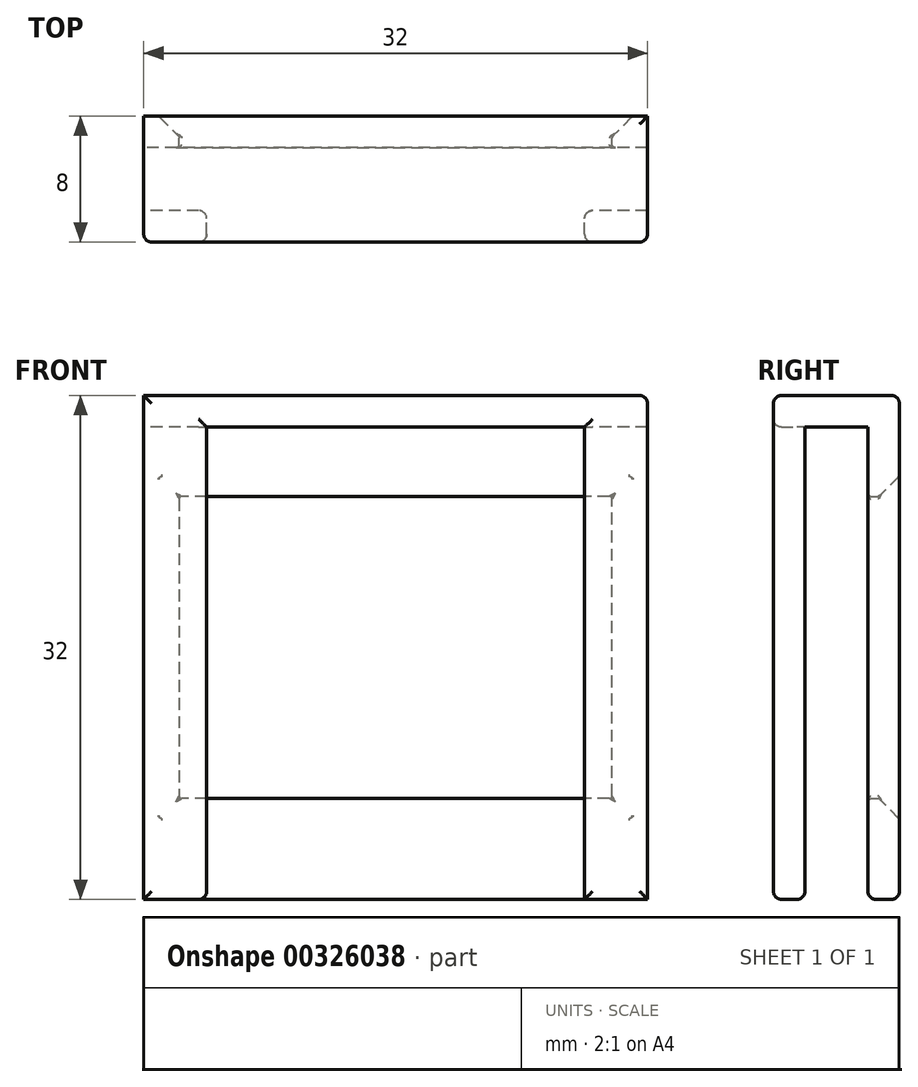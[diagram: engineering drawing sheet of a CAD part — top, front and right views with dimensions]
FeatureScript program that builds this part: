
annotation { "Feature Type Name" : "Feature", "Feature Type Description" : "" }
export const myFeature = defineFeature(function(context is Context, id is Id, definition is map)
    precondition{}
    {
        {
            var Q0;
            Q0=qCreatedBy(makeId("Front.planeOp"),FACE);
            var sketch = newSketch(context, id + "F0", { "sketchPlane" : qUnion([Q0])});
            skLineSegment(sketch, "E0.bottom", {"start": v(16, -16) * mm, "end": v(-16, -16) * mm});
            skLineSegment(sketch, "E0.top", {"start": v(16, 16) * mm, "end": v(-16, 16) * mm});
            skLineSegment(sketch, "E0.right", {"start": v(-16, -16) * mm, "end": v(-16, 16) * mm});
            skPoint(sketch, "E0.middle", {"position": v(0, 0) * mm});
            skLineSegment(sketch, "E1.0", {"start": v(16, 14) * mm, "end": v(-16, 14) * mm, "construction": true});
            skLineSegment(sketch, "E2.0", {"start": v(14, -16) * mm, "end": v(14, 16) * mm, "construction": true});
            skLineSegment(sketch, "E3.0", {"start": v(12, -16) * mm, "end": v(12, 16) * mm, "construction": true});
            skLineSegment(sketch, "E4.0", {"start": v(-14, -16) * mm, "end": v(-14, 16) * mm, "construction": true});
            skLineSegment(sketch, "E5.0", {"start": v(-12, -16) * mm, "end": v(-12, 16) * mm, "construction": true});
            skLineSegment(sketch, "E6.bottom", {"start": v(-13.75, 9.6) * mm, "end": v(13.75, 9.6) * mm});
            skLineSegment(sketch, "E6.top", {"start": v(-13.75, -9.6) * mm, "end": v(13.75, -9.6) * mm});
            skLineSegment(sketch, "E6.left", {"start": v(-13.75, 9.6) * mm, "end": v(-13.75, -9.6) * mm});
            skLineSegment(sketch, "E6.right", {"start": v(13.75, 9.6) * mm, "end": v(13.75, -9.6) * mm});
            skLineSegment(sketch, "E7", {"start": v(16, -16) * mm, "end": v(16, 16) * mm});
            skLineSegment(sketch, "E8.top", {"start": v(16, 14) * mm, "end": v(-16, 14) * mm});
            skLineSegment(sketch, "E8.left", {"start": v(16, 16) * mm, "end": v(16, 14) * mm});
            skLineSegment(sketch, "E8.right", {"start": v(-16, 16) * mm, "end": v(-16, 14) * mm});
            skLineSegment(sketch, "E9.bottom", {"start": v(-14, 16) * mm, "end": v(-16, 16) * mm});
            skLineSegment(sketch, "E9.top", {"start": v(-14, -16) * mm, "end": v(-16, -16) * mm});
            skLineSegment(sketch, "E9.left", {"start": v(-14, 16) * mm, "end": v(-14, -16) * mm});
            skLineSegment(sketch, "E9.right", {"start": v(-16, 16) * mm, "end": v(-16, -16) * mm});
            skLineSegment(sketch, "E10.bottom", {"start": v(16, 16) * mm, "end": v(14, 16) * mm});
            skLineSegment(sketch, "E10.top", {"start": v(16, -16) * mm, "end": v(14, -16) * mm});
            skLineSegment(sketch, "E10.left", {"start": v(16, 16) * mm, "end": v(16, -16) * mm});
            skLineSegment(sketch, "E10.right", {"start": v(14, 16) * mm, "end": v(14, -16) * mm});
            skSolve(sketch);
        }
        {
            var Q0;
            Q0=qSketchRegion(id+"F0",true);
            extrude(context, id + "F1", {"entities" : qUnion([Q0]), "depth" : 2 * mm});
        }
        {
            var Q0;
            {var subQ5=sQuery(id+"F0.wireOp",EDGE,"E10.bottom");Q0=makeQuery(id+"F0.imprint","IMPRINT",FACE,{"disambiguationData":[TD([[makeQuery(id+"F0.imprint","IMPRINT",EDGE,{"derivedFrom":subQ5}),1.0]])]});}
            var Q1;
            {var subQ5=sQuery(id+"F0.wireOp",EDGE,"E9.bottom");Q1=makeQuery(id+"F0.imprint","IMPRINT",FACE,{"disambiguationData":[TD([[makeQuery(id+"F0.imprint","IMPRINT",EDGE,{"derivedFrom":subQ5}),1.0]])]});}
            var Q2;
            {var subQ5=sQuery(id+"F0.wireOp",EDGE,"E9.top");Q2=makeQuery(id+"F0.imprint","IMPRINT",FACE,{"disambiguationData":[TD([[makeQuery(id+"F0.imprint","IMPRINT",EDGE,{"derivedFrom":subQ5}),-1.0]])]});}
            var Q3;
            {var subQ0=sQuery(id+"F0.wireOp",EDGE,"E0.top");Q3=makeQuery(id+"F0.imprint","IMPRINT",FACE,{"disambiguationData":[TD([[makeQuery(id+"F0.imprint","IMPRINT",EDGE,{"derivedFrom":subQ0}),1.0]])]});}
            var Q4;
            {var subQ5=sQuery(id+"F0.wireOp",EDGE,"E10.top");Q4=makeQuery(id+"F0.imprint","IMPRINT",FACE,{"disambiguationData":[TD([[makeQuery(id+"F0.imprint","IMPRINT",EDGE,{"derivedFrom":subQ5}),-1.0]])]});}
            extrude(context, id + "F2", {"entities" : qUnion([Q0, Q1, Q2, Q3, Q4]), "operationType" : NewBodyOperationType.ADD, "depth" : 6 * mm});
        }
        {
            var Q0;
            Q0=makeQuery(id+"F2.opExtrude","CAP_FACE",FACE,{"disambiguationData":[OSD([sQuery(id+"F0.wireOp",EDGE,"E0.top"),sQuery(id+"F0.wireOp",EDGE,"E8.top"),sQuery(id+"F0.wireOp",EDGE,"E9.bottom"),sQuery(id+"F0.wireOp",EDGE,"E9.top"),sQuery(id+"F0.wireOp",EDGE,"E9.left"),sQuery(id+"F0.wireOp",EDGE,"E9.right"),sQuery(id+"F0.wireOp",EDGE,"E10.bottom"),sQuery(id+"F0.wireOp",EDGE,"E10.top"),sQuery(id+"F0.wireOp",EDGE,"E10.left"),sQuery(id+"F0.wireOp",EDGE,"E10.right")])],"isStart":false});
            var sketch = newSketch(context, id + "F3", { "sketchPlane" : qUnion([Q0])});
            skLineSegment(sketch, "E11.bottom", {"start": v(-16, 16) * mm, "end": v(14, 16) * mm});
            skLineSegment(sketch, "E11.top", {"start": v(-12, 14) * mm, "end": v(12, 14) * mm});
            skLineSegment(sketch, "E11.left", {"start": v(-16, 16) * mm, "end": v(-16, 14) * mm});
            skLineSegment(sketch, "E12.bottom", {"start": v(16, 16) * mm, "end": v(12, 16) * mm});
            skLineSegment(sketch, "E12.top", {"start": v(16, -16) * mm, "end": v(12, -16) * mm});
            skLineSegment(sketch, "E12.left", {"start": v(16, 16) * mm, "end": v(16, -16) * mm});
            skLineSegment(sketch, "E12.right", {"start": v(12, 14) * mm, "end": v(12, -16) * mm});
            skLineSegment(sketch, "E13.bottom", {"start": v(-16, -16) * mm, "end": v(-12, -16) * mm});
            skLineSegment(sketch, "E13.top", {"start": v(-16, 16) * mm, "end": v(-12, 16) * mm});
            skLineSegment(sketch, "E13.left", {"start": v(-16, -16) * mm, "end": v(-16, 16) * mm});
            skLineSegment(sketch, "E13.right", {"start": v(-12, -16) * mm, "end": v(-12, 14) * mm});
            skSolve(sketch);
        }
        {
            var Q0;
            Q0=qSketchRegion(id+"F3",true);
            extrude(context, id + "F4", {"entities" : qUnion([Q0]), "operationType" : NewBodyOperationType.ADD, "depth" : 2 * mm});
        }
        {
            var Q0;
            Q0=makeQuery(id+"F4.opExtrude","CAP_FACE",FACE,{"disambiguationData":[OSD([sQuery(id+"F3.wireOp",EDGE,"E11.bottom"),sQuery(id+"F3.wireOp",EDGE,"E11.top"),sQuery(id+"F3.wireOp",EDGE,"E12.bottom"),sQuery(id+"F3.wireOp",EDGE,"E12.top"),sQuery(id+"F3.wireOp",EDGE,"E12.left"),sQuery(id+"F3.wireOp",EDGE,"E12.right"),sQuery(id+"F3.wireOp",EDGE,"E13.bottom"),sQuery(id+"F3.wireOp",EDGE,"E13.top"),sQuery(id+"F3.wireOp",EDGE,"E13.left"),sQuery(id+"F3.wireOp",EDGE,"E13.right")])],"isStart":false});
            var Q1;
            Q1=makeQuery(id+"F4.opExtrude","CAP_EDGE",EDGE,{"disambiguationData":[OSD([sQuery(id+"F3.wireOp",EDGE,"E13.right")])],"isStart":true});
            var Q2;
            Q2=makeQuery(id+"F4.opExtrude","CAP_EDGE",EDGE,{"disambiguationData":[OSD([sQuery(id+"F3.wireOp",EDGE,"E12.right")])],"isStart":true});
            var Q3;
            Q3=makeQuery(id+"F4.opExtrude","CAP_EDGE",EDGE,{"disambiguationData":[OSD([sQuery(id+"F3.wireOp",EDGE,"E12.top")])],"isStart":true});
            var Q4;
            {var subQ0=sQuery(id+"F0.wireOp",EDGE,"E10.left");var subQ1=sQuery(id+"F0.wireOp",EDGE,"E10.top");Q4=makeQuery(id+"F4.boolean.opBoolean","MERGE",EDGE,{"derivedFrom":[makeQuery(id+"F2.boolean.opBoolean","MERGE",EDGE,{"derivedFrom":[makeQuery(id+"F1.opExtrude","SWEPT_EDGE",EDGE,{"disambiguationData":[OSD([subQ1,subQ0])]}),makeQuery(id+"F2.opExtrude","SWEPT_EDGE",EDGE,{"disambiguationData":[OSD([subQ1,subQ0])]})]}),makeQuery(id+"F4.opExtrude","SWEPT_EDGE",EDGE,{"disambiguationData":[OSD([sQuery(id+"F3.wireOp",EDGE,"E12.top"),sQuery(id+"F3.wireOp",EDGE,"E12.left")])]})]});}
            var Q5;
            Q5=makeQuery(id+"F1.opExtrude","CAP_EDGE",EDGE,{"disambiguationData":[OSD([sQuery(id+"F0.wireOp",EDGE,"E0.bottom"),sQuery(id+"F0.wireOp",EDGE,"E9.top"),sQuery(id+"F0.wireOp",EDGE,"E10.top")])],"isStart":true});
            var Q6;
            Q6=makeQuery(id+"F1.opExtrude","CAP_EDGE",EDGE,{"disambiguationData":[OSD([sQuery(id+"F0.wireOp",EDGE,"E0.bottom"),sQuery(id+"F0.wireOp",EDGE,"E9.top"),sQuery(id+"F0.wireOp",EDGE,"E10.top")])],"isStart":false});
            var Q7;
            Q7=makeQuery(id+"F2.opExtrude","SWEPT_EDGE",EDGE,{"disambiguationData":[OSD([sQuery(id+"F0.wireOp",EDGE,"E0.bottom"),sQuery(id+"F0.wireOp",EDGE,"E9.top"),sQuery(id+"F0.wireOp",EDGE,"E9.left")])]});
            var Q8;
            Q8=makeQuery(id+"F4.opExtrude","CAP_EDGE",EDGE,{"disambiguationData":[OSD([sQuery(id+"F3.wireOp",EDGE,"E13.bottom")])],"isStart":true});
            var Q9;
            Q9=makeQuery(id+"F4.opExtrude","SWEPT_EDGE",EDGE,{"disambiguationData":[OSD([sQuery(id+"F3.wireOp",EDGE,"E13.bottom"),sQuery(id+"F3.wireOp",EDGE,"E13.right")])]});
            var Q10;
            {var subQ0=sQuery(id+"F0.wireOp",EDGE,"E9.right");var subQ1=sQuery(id+"F0.wireOp",EDGE,"E9.top");Q10=makeQuery(id+"F4.boolean.opBoolean","MERGE",EDGE,{"derivedFrom":[makeQuery(id+"F2.boolean.opBoolean","MERGE",EDGE,{"derivedFrom":[makeQuery(id+"F1.opExtrude","SWEPT_EDGE",EDGE,{"disambiguationData":[OSD([subQ1,subQ0])]}),makeQuery(id+"F2.opExtrude","SWEPT_EDGE",EDGE,{"disambiguationData":[OSD([subQ1,subQ0])]})]}),makeQuery(id+"F4.opExtrude","SWEPT_EDGE",EDGE,{"disambiguationData":[OSD([sQuery(id+"F3.wireOp",EDGE,"E13.bottom"),sQuery(id+"F3.wireOp",EDGE,"E13.left")])]})]});}
            var Q11;
            {var subQ0=sQuery(id+"F0.wireOp",EDGE,"E10.left");var subQ1=sQuery(id+"F0.wireOp",EDGE,"E10.bottom");Q11=makeQuery(id+"F4.boolean.opBoolean","MERGE",EDGE,{"derivedFrom":[makeQuery(id+"F2.boolean.opBoolean","MERGE",EDGE,{"derivedFrom":[makeQuery(id+"F1.opExtrude","SWEPT_EDGE",EDGE,{"disambiguationData":[OSD([subQ1,subQ0])]}),makeQuery(id+"F2.opExtrude","SWEPT_EDGE",EDGE,{"disambiguationData":[OSD([subQ1,subQ0])]})]}),makeQuery(id+"F4.opExtrude","SWEPT_EDGE",EDGE,{"disambiguationData":[OSD([sQuery(id+"F3.wireOp",EDGE,"E12.bottom"),sQuery(id+"F3.wireOp",EDGE,"E12.left")])]})]});}
            var Q12;
            {var subQ0=sQuery(id+"F0.wireOp",EDGE,"E9.right");var subQ1=sQuery(id+"F0.wireOp",EDGE,"E9.bottom");Q12=makeQuery(id+"F4.boolean.opBoolean","MERGE",EDGE,{"derivedFrom":[makeQuery(id+"F2.boolean.opBoolean","MERGE",EDGE,{"derivedFrom":[makeQuery(id+"F1.opExtrude","SWEPT_EDGE",EDGE,{"disambiguationData":[OSD([subQ1,subQ0])]}),makeQuery(id+"F2.opExtrude","SWEPT_EDGE",EDGE,{"disambiguationData":[OSD([subQ1,subQ0])]})]}),makeQuery(id+"F4.opExtrude","SWEPT_EDGE",EDGE,{"disambiguationData":[OSD([sQuery(id+"F3.wireOp",EDGE,"E13.top"),sQuery(id+"F3.wireOp",EDGE,"E13.left")])]})]});}
            var Q13;
            Q13=makeQuery(id+"F1.opExtrude","CAP_EDGE",EDGE,{"disambiguationData":[OSD([sQuery(id+"F0.wireOp",EDGE,"E0.top"),sQuery(id+"F0.wireOp",EDGE,"E9.bottom"),sQuery(id+"F0.wireOp",EDGE,"E10.bottom")])],"isStart":true});
            var Q14;
            Q14=makeQuery(id+"F1.opExtrude","CAP_EDGE",EDGE,{"disambiguationData":[OSD([sQuery(id+"F0.wireOp",EDGE,"E10.left")])],"isStart":true});
            var Q15;
            Q15=makeQuery(id+"F1.opExtrude","CAP_EDGE",EDGE,{"disambiguationData":[OSD([sQuery(id+"F0.wireOp",EDGE,"E9.right")])],"isStart":true});
            fillet(context, id + "F5", {"entities" : qUnion([Q0, Q1, Q2, Q3, Q4, Q5, Q6, Q7, Q8, Q9, Q10, Q11, Q12, Q13, Q14, Q15]), "radius" : 0.5 * mm, "tangentPropagation" : true, "allowEdgeOverflow" : false});
        }
        {
            var Q0;
            Q0=makeQuery(id+"F1.opExtrude","CAP_EDGE",EDGE,{"disambiguationData":[OSD([sQuery(id+"F0.wireOp",EDGE,"E6.top")])],"isStart":true});
            var Q1;
            Q1=makeQuery(id+"F1.opExtrude","CAP_EDGE",EDGE,{"disambiguationData":[OSD([sQuery(id+"F0.wireOp",EDGE,"E6.bottom")])],"isStart":true});
            var Q2;
            Q2=makeQuery(id+"F1.opExtrude","CAP_EDGE",EDGE,{"disambiguationData":[OSD([sQuery(id+"F0.wireOp",EDGE,"E6.left")])],"isStart":true});
            var Q3;
            Q3=makeQuery(id+"F1.opExtrude","CAP_EDGE",EDGE,{"disambiguationData":[OSD([sQuery(id+"F0.wireOp",EDGE,"E6.right")])],"isStart":true});
            chamfer(context, id + "F6", {"entities" : qUnion([Q0, Q1, Q2, Q3]), "width" : 1.3 * mm, "tangentPropagation" : true});
        }
        {
            var Q0;
            {var subQ0=sQuery(id+"F0.wireOp",EDGE,"E6.right");Q0=makeQuery(id+"F6.opChamfer","BLEND_EDGE",EDGE,{"blendedFrom":[makeQuery(id+"F1.opExtrude","CAP_EDGE",EDGE,{"disambiguationData":[OSD([subQ0])],"isStart":true}),makeQuery(id+"F1.opExtrude","CAP_FACE",FACE,{"disambiguationData":[OSD([sQuery(id+"F0.wireOp",EDGE,"E0.bottom"),sQuery(id+"F0.wireOp",EDGE,"E6.bottom"),sQuery(id+"F0.wireOp",EDGE,"E6.top"),sQuery(id+"F0.wireOp",EDGE,"E6.left"),subQ0,sQuery(id+"F0.wireOp",EDGE,"E0.top"),sQuery(id+"F0.wireOp",EDGE,"E9.bottom"),sQuery(id+"F0.wireOp",EDGE,"E9.top"),sQuery(id+"F0.wireOp",EDGE,"E9.right"),sQuery(id+"F0.wireOp",EDGE,"E10.bottom"),sQuery(id+"F0.wireOp",EDGE,"E10.top"),sQuery(id+"F0.wireOp",EDGE,"E10.left")])],"isStart":true})],"blendedInto":[makeQuery(id+"F1.opExtrude","CAP_FACE",FACE,{"disambiguationData":[OSD([sQuery(id+"F0.wireOp",EDGE,"E0.bottom"),sQuery(id+"F0.wireOp",EDGE,"E6.bottom"),sQuery(id+"F0.wireOp",EDGE,"E6.top"),sQuery(id+"F0.wireOp",EDGE,"E6.left"),subQ0,sQuery(id+"F0.wireOp",EDGE,"E0.top"),sQuery(id+"F0.wireOp",EDGE,"E9.bottom"),sQuery(id+"F0.wireOp",EDGE,"E9.top"),sQuery(id+"F0.wireOp",EDGE,"E9.right"),sQuery(id+"F0.wireOp",EDGE,"E10.bottom"),sQuery(id+"F0.wireOp",EDGE,"E10.top"),sQuery(id+"F0.wireOp",EDGE,"E10.left")])],"isStart":true})]});}
            var Q1;
            {var subQ0=sQuery(id+"F0.wireOp",EDGE,"E6.bottom");Q1=makeQuery(id+"F6.opChamfer","BLEND_EDGE",EDGE,{"blendedFrom":[makeQuery(id+"F1.opExtrude","CAP_EDGE",EDGE,{"disambiguationData":[OSD([subQ0])],"isStart":true}),makeQuery(id+"F1.opExtrude","CAP_FACE",FACE,{"disambiguationData":[OSD([sQuery(id+"F0.wireOp",EDGE,"E0.bottom"),subQ0,sQuery(id+"F0.wireOp",EDGE,"E6.top"),sQuery(id+"F0.wireOp",EDGE,"E6.left"),sQuery(id+"F0.wireOp",EDGE,"E6.right"),sQuery(id+"F0.wireOp",EDGE,"E0.top"),sQuery(id+"F0.wireOp",EDGE,"E9.bottom"),sQuery(id+"F0.wireOp",EDGE,"E9.top"),sQuery(id+"F0.wireOp",EDGE,"E9.right"),sQuery(id+"F0.wireOp",EDGE,"E10.bottom"),sQuery(id+"F0.wireOp",EDGE,"E10.top"),sQuery(id+"F0.wireOp",EDGE,"E10.left")])],"isStart":true})],"blendedInto":[makeQuery(id+"F1.opExtrude","CAP_FACE",FACE,{"disambiguationData":[OSD([sQuery(id+"F0.wireOp",EDGE,"E0.bottom"),subQ0,sQuery(id+"F0.wireOp",EDGE,"E6.top"),sQuery(id+"F0.wireOp",EDGE,"E6.left"),sQuery(id+"F0.wireOp",EDGE,"E6.right"),sQuery(id+"F0.wireOp",EDGE,"E0.top"),sQuery(id+"F0.wireOp",EDGE,"E9.bottom"),sQuery(id+"F0.wireOp",EDGE,"E9.top"),sQuery(id+"F0.wireOp",EDGE,"E9.right"),sQuery(id+"F0.wireOp",EDGE,"E10.bottom"),sQuery(id+"F0.wireOp",EDGE,"E10.top"),sQuery(id+"F0.wireOp",EDGE,"E10.left")])],"isStart":true})]});}
            var Q2;
            {var subQ0=sQuery(id+"F0.wireOp",EDGE,"E6.left");Q2=makeQuery(id+"F6.opChamfer","BLEND_EDGE",EDGE,{"blendedFrom":[makeQuery(id+"F1.opExtrude","CAP_EDGE",EDGE,{"disambiguationData":[OSD([subQ0])],"isStart":true}),makeQuery(id+"F1.opExtrude","CAP_FACE",FACE,{"disambiguationData":[OSD([sQuery(id+"F0.wireOp",EDGE,"E0.bottom"),sQuery(id+"F0.wireOp",EDGE,"E6.bottom"),sQuery(id+"F0.wireOp",EDGE,"E6.top"),subQ0,sQuery(id+"F0.wireOp",EDGE,"E6.right"),sQuery(id+"F0.wireOp",EDGE,"E0.top"),sQuery(id+"F0.wireOp",EDGE,"E9.bottom"),sQuery(id+"F0.wireOp",EDGE,"E9.top"),sQuery(id+"F0.wireOp",EDGE,"E9.right"),sQuery(id+"F0.wireOp",EDGE,"E10.bottom"),sQuery(id+"F0.wireOp",EDGE,"E10.top"),sQuery(id+"F0.wireOp",EDGE,"E10.left")])],"isStart":true})],"blendedInto":[makeQuery(id+"F1.opExtrude","CAP_FACE",FACE,{"disambiguationData":[OSD([sQuery(id+"F0.wireOp",EDGE,"E0.bottom"),sQuery(id+"F0.wireOp",EDGE,"E6.bottom"),sQuery(id+"F0.wireOp",EDGE,"E6.top"),subQ0,sQuery(id+"F0.wireOp",EDGE,"E6.right"),sQuery(id+"F0.wireOp",EDGE,"E0.top"),sQuery(id+"F0.wireOp",EDGE,"E9.bottom"),sQuery(id+"F0.wireOp",EDGE,"E9.top"),sQuery(id+"F0.wireOp",EDGE,"E9.right"),sQuery(id+"F0.wireOp",EDGE,"E10.bottom"),sQuery(id+"F0.wireOp",EDGE,"E10.top"),sQuery(id+"F0.wireOp",EDGE,"E10.left")])],"isStart":true})]});}
            var Q3;
            {var subQ0=sQuery(id+"F0.wireOp",EDGE,"E6.top");Q3=makeQuery(id+"F6.opChamfer","BLEND_EDGE",EDGE,{"blendedFrom":[makeQuery(id+"F1.opExtrude","CAP_EDGE",EDGE,{"disambiguationData":[OSD([subQ0])],"isStart":true}),makeQuery(id+"F1.opExtrude","CAP_FACE",FACE,{"disambiguationData":[OSD([sQuery(id+"F0.wireOp",EDGE,"E0.bottom"),sQuery(id+"F0.wireOp",EDGE,"E6.bottom"),subQ0,sQuery(id+"F0.wireOp",EDGE,"E6.left"),sQuery(id+"F0.wireOp",EDGE,"E6.right"),sQuery(id+"F0.wireOp",EDGE,"E0.top"),sQuery(id+"F0.wireOp",EDGE,"E9.bottom"),sQuery(id+"F0.wireOp",EDGE,"E9.top"),sQuery(id+"F0.wireOp",EDGE,"E9.right"),sQuery(id+"F0.wireOp",EDGE,"E10.bottom"),sQuery(id+"F0.wireOp",EDGE,"E10.top"),sQuery(id+"F0.wireOp",EDGE,"E10.left")])],"isStart":true})],"blendedInto":[makeQuery(id+"F1.opExtrude","CAP_FACE",FACE,{"disambiguationData":[OSD([sQuery(id+"F0.wireOp",EDGE,"E0.bottom"),sQuery(id+"F0.wireOp",EDGE,"E6.bottom"),subQ0,sQuery(id+"F0.wireOp",EDGE,"E6.left"),sQuery(id+"F0.wireOp",EDGE,"E6.right"),sQuery(id+"F0.wireOp",EDGE,"E0.top"),sQuery(id+"F0.wireOp",EDGE,"E9.bottom"),sQuery(id+"F0.wireOp",EDGE,"E9.top"),sQuery(id+"F0.wireOp",EDGE,"E9.right"),sQuery(id+"F0.wireOp",EDGE,"E10.bottom"),sQuery(id+"F0.wireOp",EDGE,"E10.top"),sQuery(id+"F0.wireOp",EDGE,"E10.left")])],"isStart":true})]});}
            var Q4;
            Q4=makeQuery(id+"F6.opChamfer","BLEND_EDGE",EDGE,{"blendedFrom":[makeQuery(id+"F1.opExtrude","CAP_EDGE",EDGE,{"disambiguationData":[OSD([sQuery(id+"F0.wireOp",EDGE,"E6.top")])],"isStart":true}),makeQuery(id+"F1.opExtrude","CAP_EDGE",EDGE,{"disambiguationData":[OSD([sQuery(id+"F0.wireOp",EDGE,"E6.left")])],"isStart":true})],"blendedInto":[]});
            var Q5;
            Q5=makeQuery(id+"F6.opChamfer","BLEND_EDGE",EDGE,{"blendedFrom":[makeQuery(id+"F1.opExtrude","CAP_EDGE",EDGE,{"disambiguationData":[OSD([sQuery(id+"F0.wireOp",EDGE,"E6.top")])],"isStart":true}),makeQuery(id+"F1.opExtrude","CAP_EDGE",EDGE,{"disambiguationData":[OSD([sQuery(id+"F0.wireOp",EDGE,"E6.right")])],"isStart":true})],"blendedInto":[]});
            var Q6;
            Q6=makeQuery(id+"F6.opChamfer","BLEND_EDGE",EDGE,{"blendedFrom":[makeQuery(id+"F1.opExtrude","CAP_EDGE",EDGE,{"disambiguationData":[OSD([sQuery(id+"F0.wireOp",EDGE,"E6.bottom")])],"isStart":true}),makeQuery(id+"F1.opExtrude","CAP_EDGE",EDGE,{"disambiguationData":[OSD([sQuery(id+"F0.wireOp",EDGE,"E6.left")])],"isStart":true})],"blendedInto":[]});
            var Q7;
            Q7=makeQuery(id+"F6.opChamfer","BLEND_EDGE",EDGE,{"blendedFrom":[makeQuery(id+"F1.opExtrude","CAP_EDGE",EDGE,{"disambiguationData":[OSD([sQuery(id+"F0.wireOp",EDGE,"E6.bottom")])],"isStart":true}),makeQuery(id+"F1.opExtrude","CAP_EDGE",EDGE,{"disambiguationData":[OSD([sQuery(id+"F0.wireOp",EDGE,"E6.right")])],"isStart":true})],"blendedInto":[]});
            fillet(context, id + "F7", {"entities" : qUnion([Q0, Q1, Q2, Q3, Q4, Q5, Q6, Q7]), "radius" : 0.2 * mm, "tangentPropagation" : true, "allowEdgeOverflow" : false});
        }
        {
            var Q0;
            Q0=makeQuery(id+"F1.opExtrude","CAP_EDGE",EDGE,{"disambiguationData":[OSD([sQuery(id+"F0.wireOp",EDGE,"E6.left")])],"isStart":false});
            var Q1;
            Q1=makeQuery(id+"F1.opExtrude","CAP_EDGE",EDGE,{"disambiguationData":[OSD([sQuery(id+"F0.wireOp",EDGE,"E6.right")])],"isStart":false});
            var Q2;
            Q2=makeQuery(id+"F1.opExtrude","CAP_EDGE",EDGE,{"disambiguationData":[OSD([sQuery(id+"F0.wireOp",EDGE,"E6.top")])],"isStart":false});
            var Q3;
            Q3=makeQuery(id+"F1.opExtrude","CAP_EDGE",EDGE,{"disambiguationData":[OSD([sQuery(id+"F0.wireOp",EDGE,"E6.bottom")])],"isStart":false});
            var Q4;
            {var subQ0=sQuery(id+"F0.wireOp",EDGE,"E6.left");Q4=makeQuery(id+"F6.opChamfer","BLEND_EDGE",EDGE,{"blendedFrom":[makeQuery(id+"F1.opExtrude","CAP_EDGE",EDGE,{"disambiguationData":[OSD([subQ0])],"isStart":true}),makeQuery(id+"F1.opExtrude","SWEPT_FACE",FACE,{"disambiguationData":[OSD([subQ0])]})],"blendedInto":[makeQuery(id+"F1.opExtrude","SWEPT_FACE",FACE,{"disambiguationData":[OSD([subQ0])]})]});}
            var Q5;
            {var subQ0=sQuery(id+"F0.wireOp",EDGE,"E6.top");Q5=makeQuery(id+"F6.opChamfer","BLEND_EDGE",EDGE,{"blendedFrom":[makeQuery(id+"F1.opExtrude","CAP_EDGE",EDGE,{"disambiguationData":[OSD([subQ0])],"isStart":true}),makeQuery(id+"F1.opExtrude","SWEPT_FACE",FACE,{"disambiguationData":[OSD([subQ0])]})],"blendedInto":[makeQuery(id+"F1.opExtrude","SWEPT_FACE",FACE,{"disambiguationData":[OSD([subQ0])]})]});}
            var Q6;
            {var subQ0=sQuery(id+"F0.wireOp",EDGE,"E6.right");Q6=makeQuery(id+"F6.opChamfer","BLEND_EDGE",EDGE,{"blendedFrom":[makeQuery(id+"F1.opExtrude","CAP_EDGE",EDGE,{"disambiguationData":[OSD([subQ0])],"isStart":true}),makeQuery(id+"F1.opExtrude","SWEPT_FACE",FACE,{"disambiguationData":[OSD([subQ0])]})],"blendedInto":[makeQuery(id+"F1.opExtrude","SWEPT_FACE",FACE,{"disambiguationData":[OSD([subQ0])]})]});}
            var Q7;
            {var subQ0=sQuery(id+"F0.wireOp",EDGE,"E6.bottom");Q7=makeQuery(id+"F6.opChamfer","BLEND_EDGE",EDGE,{"blendedFrom":[makeQuery(id+"F1.opExtrude","CAP_EDGE",EDGE,{"disambiguationData":[OSD([subQ0])],"isStart":true}),makeQuery(id+"F1.opExtrude","SWEPT_FACE",FACE,{"disambiguationData":[OSD([subQ0])]})],"blendedInto":[makeQuery(id+"F1.opExtrude","SWEPT_FACE",FACE,{"disambiguationData":[OSD([subQ0])]})]});}
            fillet(context, id + "F8", {"entities" : qUnion([Q0, Q1, Q2, Q3, Q4, Q5, Q6, Q7]), "radius" : .2 * mm, "tangentPropagation" : true, "allowEdgeOverflow" : false});
        }
        {
            var Q0;
            Q0=makeQuery(id+"F1.opExtrude","SWEPT_EDGE",EDGE,{"disambiguationData":[OSD([sQuery(id+"F0.wireOp",EDGE,"E6.bottom"),sQuery(id+"F0.wireOp",EDGE,"E6.left")])]});
            var Q1;
            Q1=makeQuery(id+"F1.opExtrude","SWEPT_EDGE",EDGE,{"disambiguationData":[OSD([sQuery(id+"F0.wireOp",EDGE,"E6.bottom"),sQuery(id+"F0.wireOp",EDGE,"E6.right")])]});
            var Q2;
            Q2=makeQuery(id+"F1.opExtrude","SWEPT_EDGE",EDGE,{"disambiguationData":[OSD([sQuery(id+"F0.wireOp",EDGE,"E6.top"),sQuery(id+"F0.wireOp",EDGE,"E6.right")])]});
            var Q3;
            Q3=makeQuery(id+"F1.opExtrude","SWEPT_EDGE",EDGE,{"disambiguationData":[OSD([sQuery(id+"F0.wireOp",EDGE,"E6.top"),sQuery(id+"F0.wireOp",EDGE,"E6.left")])]});
            fillet(context, id + "F9", {"entities" : qUnion([Q0, Q1, Q2, Q3]), "radius" : 0.17 * mm, "tangentPropagation" : true, "allowEdgeOverflow" : false});
        }
    });
